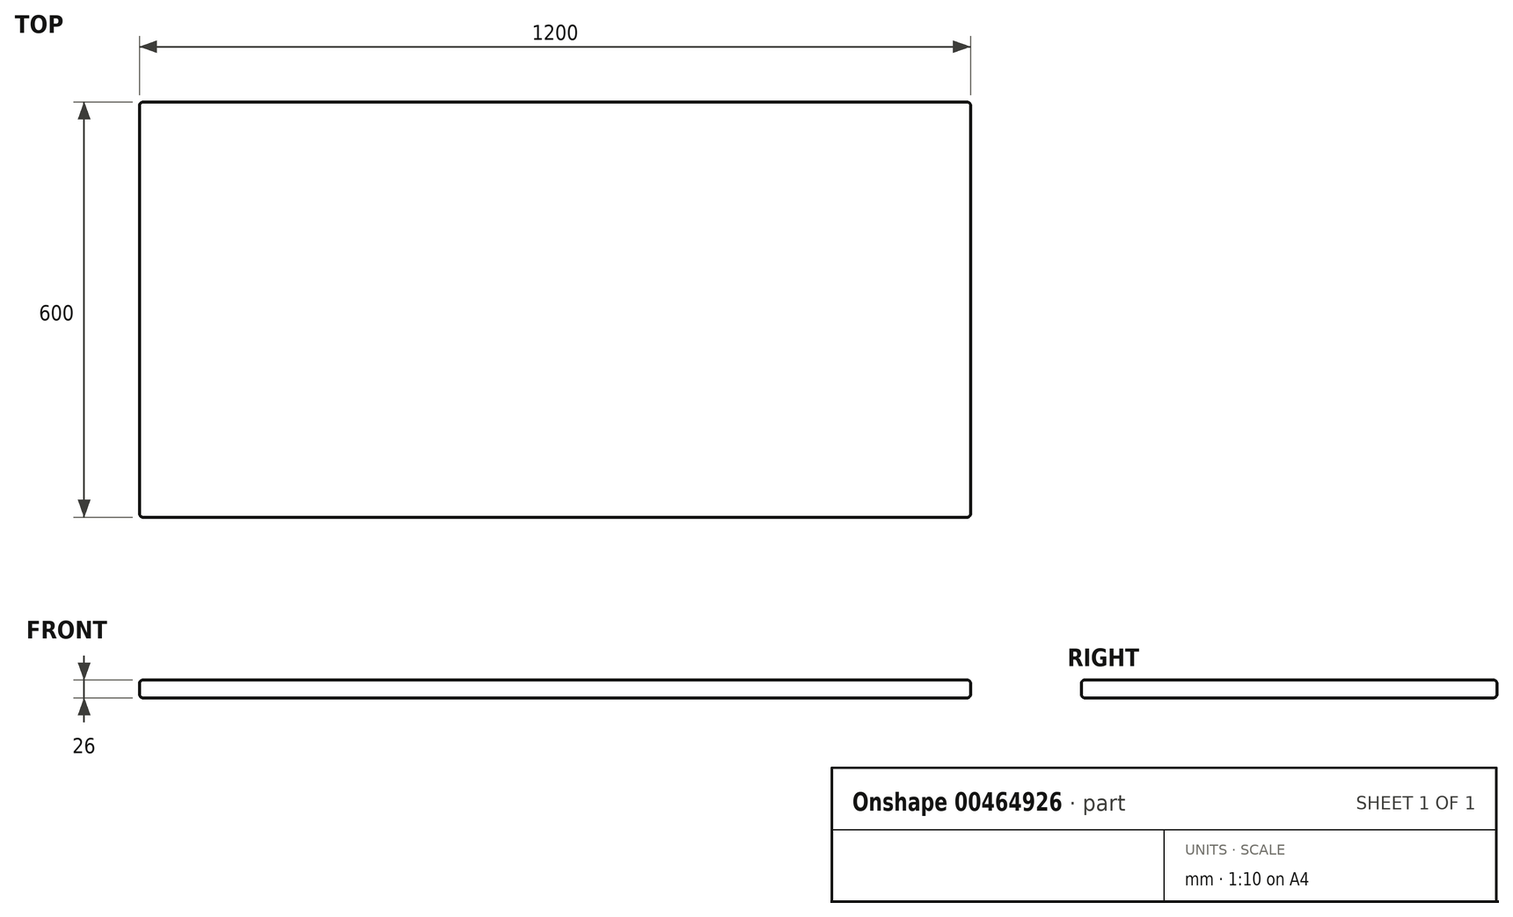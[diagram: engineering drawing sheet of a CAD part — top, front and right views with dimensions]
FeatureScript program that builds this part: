
annotation { "Feature Type Name" : "Feature", "Feature Type Description" : "" }
export const myFeature = defineFeature(function(context is Context, id is Id, definition is map)
    precondition{}
    {
        {
            var Q0;
            Q0=qCreatedBy(makeId("Top.planeOp"),FACE);
            var sketch = newSketch(context, id + "F0", { "sketchPlane" : qUnion([Q0])});
            skLineSegment(sketch, "E0.bottom", {"start": v(-600, -300) * mm, "end": v(600, -300) * mm});
            skLineSegment(sketch, "E0.top", {"start": v(-600, 300) * mm, "end": v(600, 300) * mm});
            skLineSegment(sketch, "E0.left", {"start": v(-600, -300) * mm, "end": v(-600, 300) * mm});
            skLineSegment(sketch, "E0.right", {"start": v(600, -300) * mm, "end": v(600, 300) * mm});
            skPoint(sketch, "E0.middle", {"position": v(0, 0) * mm});
            skLineSegment(sketch, "E1", {"start": v(-600, 0) * mm, "end": v(600, 0) * mm, "construction": true});
            skSolve(sketch);
        }
        {
            var Q0;
            Q0=makeQuery(id+"F0.imprint","IMPRINT",FACE,{"disambiguationData":[TD([[makeQuery(id+"F0.imprint","IMPRINT",EDGE,{"derivedFrom":sQuery(id+"F0.wireOp",EDGE,"E0.bottom")}),1.0]])]});
            extrude(context, id + "F1", {"entities" : qUnion([Q0]), "depth" : 26 * mm, "offsetDistance" : 25 * mm});
        }
        {
            var Q0;
            Q0=makeQuery(id+"F1.opExtrude","CAP_FACE",FACE,{"disambiguationData":[OSD([sQuery(id+"F0.wireOp",EDGE,"E0.bottom"),sQuery(id+"F0.wireOp",EDGE,"E0.top"),sQuery(id+"F0.wireOp",EDGE,"E0.left"),sQuery(id+"F0.wireOp",EDGE,"E0.right")])],"isStart":false});
            var Q1;
            Q1=makeQuery(id+"F1.opExtrude","CAP_FACE",FACE,{"disambiguationData":[OSD([sQuery(id+"F0.wireOp",EDGE,"E0.bottom"),sQuery(id+"F0.wireOp",EDGE,"E0.top"),sQuery(id+"F0.wireOp",EDGE,"E0.left"),sQuery(id+"F0.wireOp",EDGE,"E0.right")])],"isStart":true});
            var Q2;
            Q2=makeQuery(id+"F1.opExtrude","SWEPT_EDGE",EDGE,{"disambiguationData":[OSD([sQuery(id+"F0.wireOp",EDGE,"E0.bottom"),sQuery(id+"F0.wireOp",EDGE,"E0.left")])]});
            var Q3;
            Q3=makeQuery(id+"F1.opExtrude","SWEPT_EDGE",EDGE,{"disambiguationData":[OSD([sQuery(id+"F0.wireOp",EDGE,"E0.top"),sQuery(id+"F0.wireOp",EDGE,"E0.left")])]});
            var Q4;
            Q4=makeQuery(id+"F1.opExtrude","SWEPT_EDGE",EDGE,{"disambiguationData":[OSD([sQuery(id+"F0.wireOp",EDGE,"E0.top"),sQuery(id+"F0.wireOp",EDGE,"E0.right")])]});
            var Q5;
            Q5=makeQuery(id+"F1.opExtrude","SWEPT_EDGE",EDGE,{"disambiguationData":[OSD([sQuery(id+"F0.wireOp",EDGE,"E0.bottom"),sQuery(id+"F0.wireOp",EDGE,"E0.right")])]});
            fillet(context, id + "F2", {"entities" : qUnion([Q0, Q1, Q2, Q3, Q4, Q5]), "radius" : 5 * mm, "tangentPropagation" : true, "allowEdgeOverflow" : false});
        }
    });
